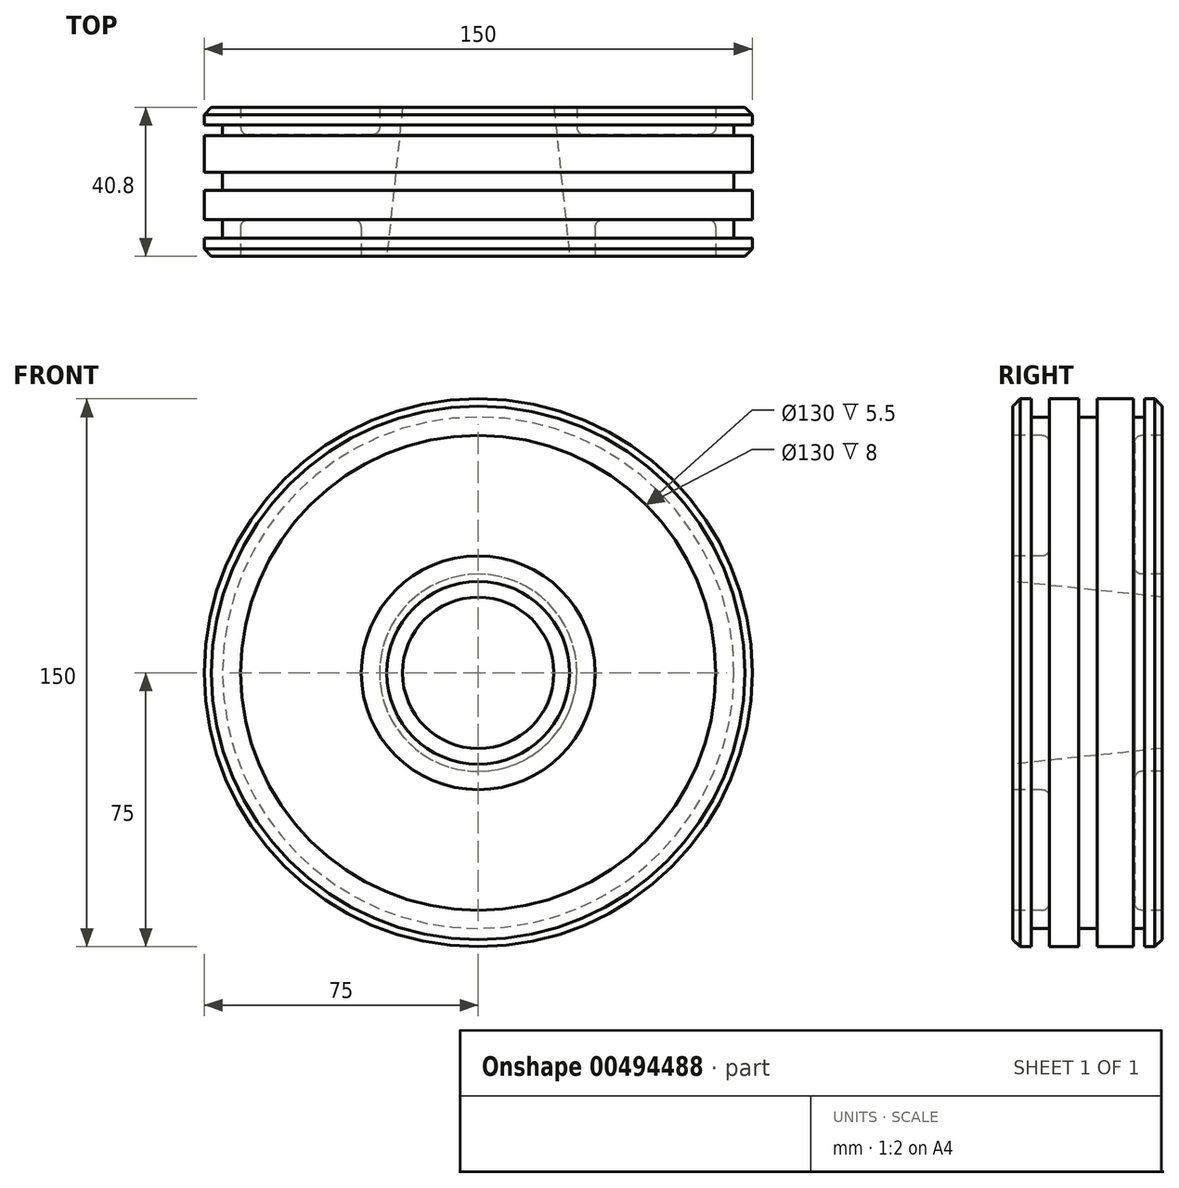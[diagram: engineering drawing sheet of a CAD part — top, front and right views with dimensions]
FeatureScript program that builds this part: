
annotation { "Feature Type Name" : "Feature", "Feature Type Description" : "" }
export const myFeature = defineFeature(function(context is Context, id is Id, definition is map)
    precondition{}
    {
        {
            var Q0;
            Q0=qCreatedBy(makeId("Right.planeOp"),FACE);
            var sketch = newSketch(context, id + "F0", { "sketchPlane" : qUnion([Q0])});
            skLineSegment(sketch, "E0.bottom", {"start": v(0, 75) * mm, "end": v(5, 75) * mm});
            skLineSegment(sketch, "E0.top", {"start": v(0, 25) * mm, "end": v(40.8, 20.71) * mm});
            skLineSegment(sketch, "E0.left", {"start": v(0, 75) * mm, "end": v(0, 25) * mm});
            skLineSegment(sketch, "E0.right", {"start": v(40.8, 75) * mm, "end": v(40.8, 20.71) * mm});
            skLineSegment(sketch, "E1.top", {"start": v(5, 70) * mm, "end": v(10, 70) * mm});
            skLineSegment(sketch, "E1.left", {"start": v(5, 75) * mm, "end": v(5, 70) * mm});
            skLineSegment(sketch, "E1.right", {"start": v(10, 75) * mm, "end": v(10, 70) * mm});
            skLineSegment(sketch, "E2.top", {"start": v(18, 70) * mm, "end": v(23, 70) * mm});
            skLineSegment(sketch, "E2.left", {"start": v(18, 75) * mm, "end": v(18, 70) * mm});
            skLineSegment(sketch, "E2.right", {"start": v(23, 75) * mm, "end": v(23, 70) * mm});
            skLineSegment(sketch, "E3.top", {"start": v(33, 70) * mm, "end": v(36, 70) * mm});
            skLineSegment(sketch, "E3.left", {"start": v(33, 75) * mm, "end": v(33, 70) * mm});
            skLineSegment(sketch, "E3.right", {"start": v(36, 75) * mm, "end": v(36, 70) * mm});
            skLineSegment(sketch, "E4.trimOffspring", {"start": v(10, 75) * mm, "end": v(18, 75) * mm});
            skLineSegment(sketch, "E5.trimOffspring", {"start": v(23, 75) * mm, "end": v(33, 75) * mm});
            skLineSegment(sketch, "E6.trimOffspring", {"start": v(36, 75) * mm, "end": v(40.8, 75) * mm});
            skLineSegment(sketch, "E7.bottom", {"start": v(33.3, 65) * mm, "end": v(40.8, 65) * mm});
            skLineSegment(sketch, "E7.top", {"start": v(33.3, 27) * mm, "end": v(40.8, 27) * mm});
            skLineSegment(sketch, "E7.left", {"start": v(33.3, 65) * mm, "end": v(33.3, 27) * mm});
            skLineSegment(sketch, "E7.right", {"start": v(40.8, 65) * mm, "end": v(40.8, 27) * mm});
            skLineSegment(sketch, "E8.bottom", {"start": v(0, 65) * mm, "end": v(10, 65) * mm});
            skLineSegment(sketch, "E8.top", {"start": v(0, 32) * mm, "end": v(10, 32) * mm});
            skLineSegment(sketch, "E8.left", {"start": v(0, 65) * mm, "end": v(0, 32) * mm});
            skLineSegment(sketch, "E8.right", {"start": v(10, 65) * mm, "end": v(10, 32) * mm});
            skLineSegment(sketch, "E9", {"start": v(-83.05, 0) * mm, "end": v(119.65, 0) * mm, "construction": true});
            skSolve(sketch);
        }
        {
            var Q0;
            {var subQ8=sQuery(id+"F0.wireOp",EDGE,"E0.bottom");Q0=makeQuery(id+"F0.imprint","IMPRINT",FACE,{"disambiguationData":[TD([[makeQuery(id+"F0.imprint","IMPRINT",EDGE,{"derivedFrom":subQ8}),-1.0]])]});}
            var Q1;
            Q1=sQuery(id+"F0.wireOp",EDGE,"E9");
            revolve(context, id + "F1", {"entities" : qUnion([Q0]), "axis" : qUnion([Q1]), "revolveType" : RevolveType.FULL});
        }
        {
            var Q0;
            Q0=makeQuery(id+"F1.opRevolve","SWEPT_EDGE",EDGE,{"disambiguationData":[OSD([sQuery(id+"F0.wireOp",EDGE,"E0.right"),sQuery(id+"F0.wireOp",EDGE,"E6.trimOffspring")])]});
            var Q1;
            Q1=makeQuery(id+"F1.opRevolve","SWEPT_EDGE",EDGE,{"disambiguationData":[OSD([sQuery(id+"F0.wireOp",EDGE,"E0.bottom"),sQuery(id+"F0.wireOp",EDGE,"E0.left")])]});
            chamfer(context, id + "F2", {"entities" : qUnion([Q0, Q1]), "chamferType" : ChamferType.OFFSET_ANGLE, "width" : 2 * mm, "oppositeDirection" : false, "angle" : 45 * degree, "tangentPropagation" : true});
        }
        {
            var Q0;
            Q0=makeQuery(id+"F1.opRevolve","SWEPT_EDGE",EDGE,{"disambiguationData":[OSD([sQuery(id+"F0.wireOp",EDGE,"E8.bottom"),sQuery(id+"F0.wireOp",EDGE,"E8.right")])]});
            var Q1;
            Q1=makeQuery(id+"F1.opRevolve","SWEPT_EDGE",EDGE,{"disambiguationData":[OSD([sQuery(id+"F0.wireOp",EDGE,"E7.bottom"),sQuery(id+"F0.wireOp",EDGE,"E7.left")])]});
            var Q2;
            Q2=makeQuery(id+"F1.opRevolve","SWEPT_EDGE",EDGE,{"disambiguationData":[OSD([sQuery(id+"F0.wireOp",EDGE,"E7.top"),sQuery(id+"F0.wireOp",EDGE,"E7.left")])]});
            var Q3;
            Q3=makeQuery(id+"F1.opRevolve","SWEPT_EDGE",EDGE,{"disambiguationData":[OSD([sQuery(id+"F0.wireOp",EDGE,"E8.top"),sQuery(id+"F0.wireOp",EDGE,"E8.right")])]});
            fillet(context, id + "F3", {"entities" : qUnion([Q0, Q1, Q2, Q3]), "radius" : 2 * mm, "tangentPropagation" : true, "allowEdgeOverflow" : false});
        }
    });
